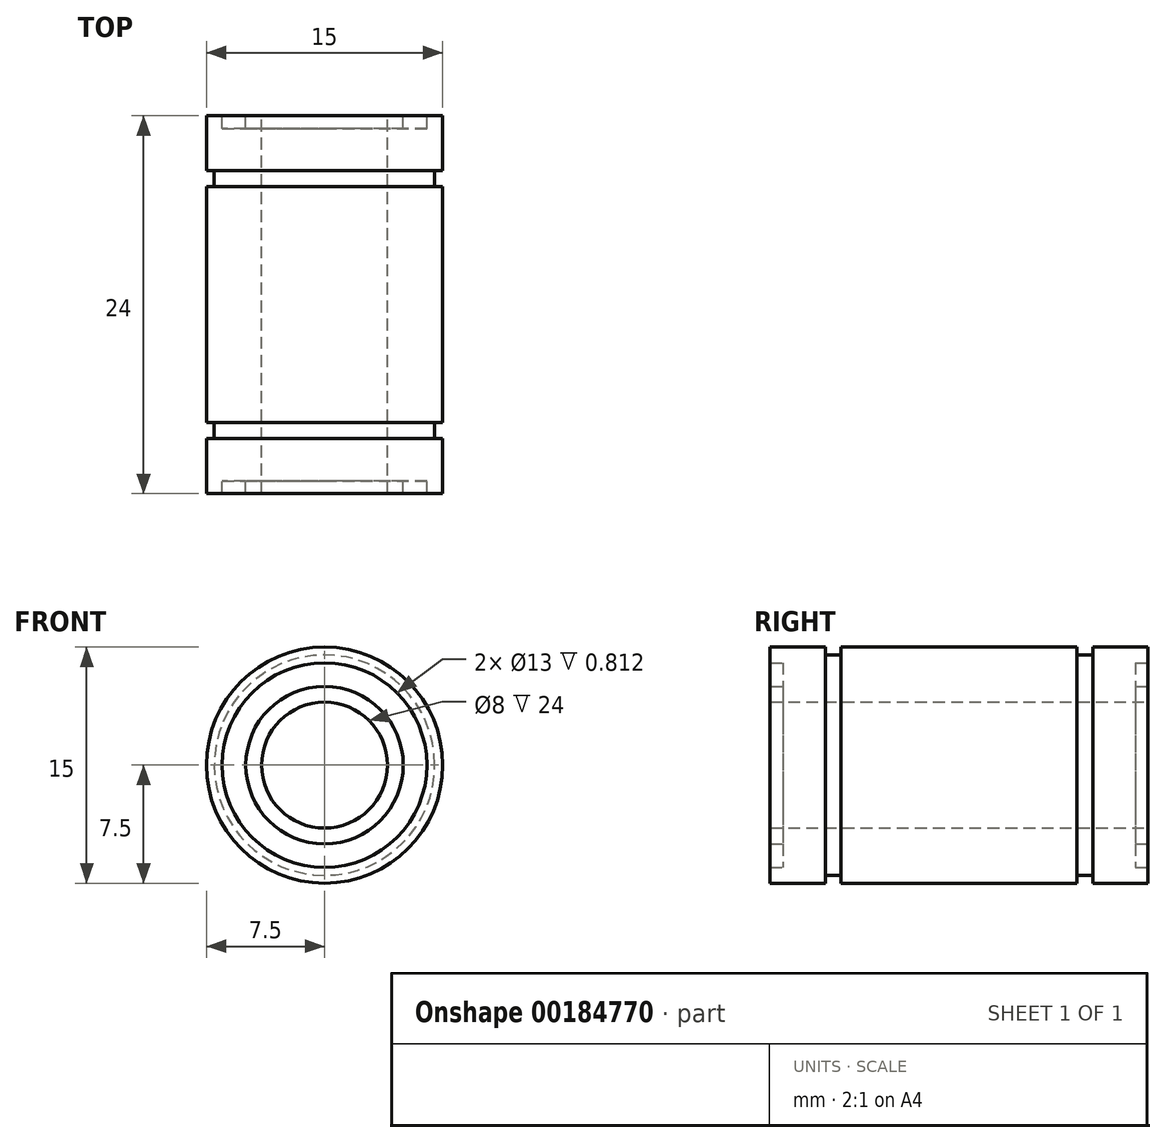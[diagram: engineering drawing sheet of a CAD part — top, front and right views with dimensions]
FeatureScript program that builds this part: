
annotation { "Feature Type Name" : "Feature", "Feature Type Description" : "" }
export const myFeature = defineFeature(function(context is Context, id is Id, definition is map)
    precondition{}
    {
        {
            var Q0;
            Q0=qCreatedBy(makeId("Top.planeOp"),FACE);
            var sketch = newSketch(context, id + "F0", { "sketchPlane" : qUnion([Q0])});
            skLineSegment(sketch, "E0", {"start": v(0, 15.08) * mm, "end": v(0, -15.96) * mm, "construction": true});
            skLineSegment(sketch, "E1.bottom", {"start": v(-7.5, 12) * mm, "end": v(-6.5, 12) * mm});
            skLineSegment(sketch, "E1.left", {"start": v(-7.5, 12) * mm, "end": v(-7.5, 8.5) * mm});
            skLineSegment(sketch, "E2.bottom", {"start": v(-7.5, 7.5) * mm, "end": v(-7, 7.5) * mm});
            skLineSegment(sketch, "E2.top", {"start": v(-7.5, 8.5) * mm, "end": v(-7, 8.5) * mm});
            skLineSegment(sketch, "E2.right", {"start": v(-7, 8.5) * mm, "end": v(-7, 7.5) * mm});
            skLineSegment(sketch, "E3.left", {"start": v(-7.5, 12) * mm, "end": v(-7.5, 11.19) * mm});
            skLineSegment(sketch, "E3.right", {"start": v(-6.5, 12) * mm, "end": v(-6.5, 11.19) * mm});
            skLineSegment(sketch, "E4", {"start": v(-6.5, 11.19) * mm, "end": v(-5, 11.19) * mm});
            skLineSegment(sketch, "E5", {"start": v(-5, 11.19) * mm, "end": v(-5, 12) * mm});
            skLineSegment(sketch, "E6", {"start": v(-5, 12) * mm, "end": v(-4, 12) * mm});
            skLineSegment(sketch, "E7", {"start": v(-4, 12) * mm, "end": v(-4, 0) * mm});
            skLineSegment(sketch, "E8.trimOffspring", {"start": v(-7.5, 7.5) * mm, "end": v(-7.5, 0) * mm});
            skLineSegment(sketch, "E9", {"start": v(0, 0) * mm, "end": v(-10.74, 0) * mm, "construction": true});
            skLineSegment(sketch, "E10.MirrorCS", {"start": v(-5, -11.19) * mm, "end": v(-5, -12) * mm});
            skLineSegment(sketch, "E11.MirrorCS", {"start": v(-7, -8.5) * mm, "end": v(-7, -7.5) * mm});
            skLineSegment(sketch, "E12.MirrorCS", {"start": v(-7.5, -8.5) * mm, "end": v(-7, -8.5) * mm});
            skLineSegment(sketch, "E13.MirrorCS", {"start": v(-6.5, -12) * mm, "end": v(-6.5, -11.19) * mm});
            skLineSegment(sketch, "E14.MirrorCS", {"start": v(-7.5, -7.5) * mm, "end": v(-7, -7.5) * mm});
            skLineSegment(sketch, "E15.MirrorCS", {"start": v(-5, -12) * mm, "end": v(-4, -12) * mm});
            skLineSegment(sketch, "E16.MirrorCS", {"start": v(-7.5, -12) * mm, "end": v(-6.5, -12) * mm});
            skLineSegment(sketch, "E17.MirrorCS", {"start": v(-7.5, -12) * mm, "end": v(-7.5, -11.19) * mm});
            skLineSegment(sketch, "E18.MirrorCS", {"start": v(-4, -12) * mm, "end": v(-4, 0) * mm});
            skLineSegment(sketch, "E19.MirrorCS", {"start": v(-7.5, -12) * mm, "end": v(-7.5, -8.5) * mm});
            skLineSegment(sketch, "E20.MirrorCS", {"start": v(-6.5, -11.19) * mm, "end": v(-5, -11.19) * mm});
            skLineSegment(sketch, "E21.MirrorCS", {"start": v(-7.5, -7.5) * mm, "end": v(-7.5, 0) * mm});
            skSolve(sketch);
        }
        {
            var Q0;
            Q0 = qSketchRegion(id + "F0", true);
            var Q1;
            Q1=sQuery(id+"F0.wireOp",EDGE,"E0");
            revolve(context, id + "F1", {"entities" : qUnion([Q0]), "axis" : qUnion([Q1]), "revolveType" : RevolveType.FULL});
        }
    });
